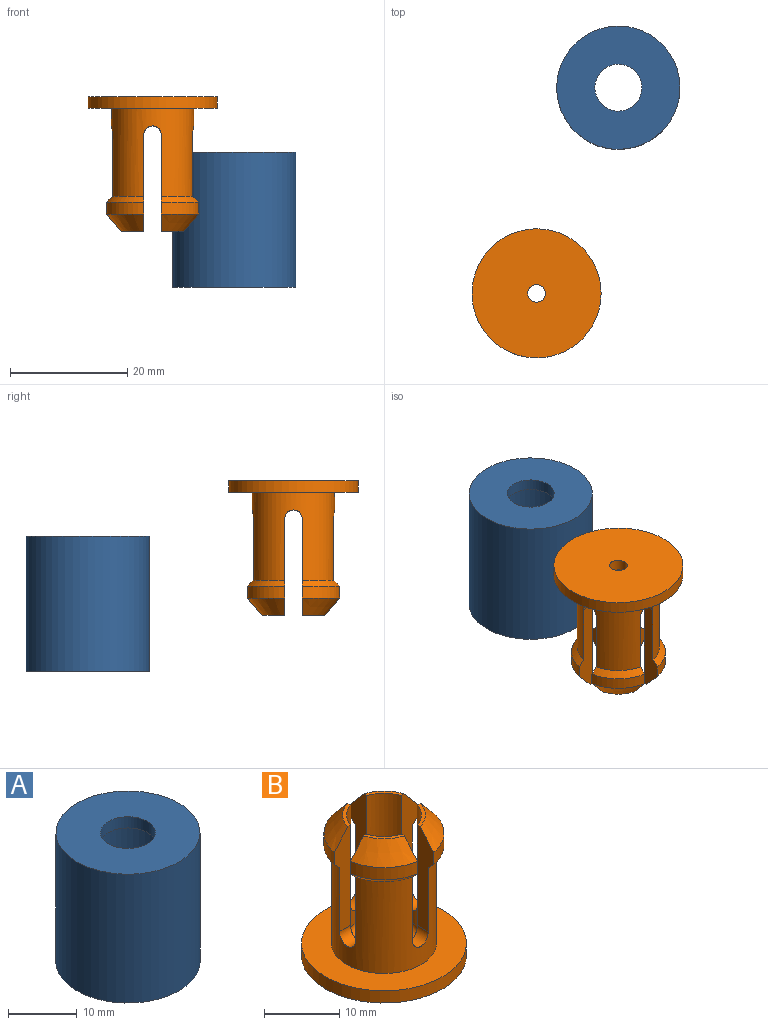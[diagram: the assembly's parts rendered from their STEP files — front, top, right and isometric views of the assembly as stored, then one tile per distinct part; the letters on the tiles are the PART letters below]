
ASSEMBLY  parts=2 mates=1
PART A: 10 faces, bbox 21x21x23 mm
  f0: cone r=7mm half-angle=45deg, axis (0,0,-1), area 103.3mm2, adj f1,f9
  f1: cylinder r=7mm len=14mm, axis (0,0,-1), area 263.9mm2, adj f0,f2
  f2: plane 14x14mm, normal (0,0,-1), area 103.7mm2, adj f1,f3
  f3: cylinder r=4mm len=8mm, axis (0,0,-1), area 50.3mm2, adj f2,f4
  f4: plane 21x21mm, normal (0,0,1), area 296.1mm2, adj f3,f5
  f5: cylinder r=10.5mm len=23mm, axis (0,0,-1), area 1517.4mm2, adj f4,f6
  f6: plane 21x21mm, normal (0,0,-1), area 192.4mm2, adj f5,f7
  f7: cylinder r=7mm len=14mm, axis (0,0,-1), area 439.8mm2, adj f6,f8
  f8: cone r=8.5mm half-angle=45deg, axis (0,0,1), area 103.3mm2, adj f7,f9
  f9: cylinder r=8.5mm len=17mm, axis (0,0,-1), area 106.8mm2, adj f0,f8
PART B: 36 faces, bbox 22.4x22.4x23.3 mm
  f0: cylinder r=5mm len=19.94mm, axis (0,0,-1), area 412mm2, adj f1,f6,f10,f14,f15,f24,f25,f26
  f1: plane 3.83x3.83mm, normal (0,0,1), area 2.8mm2, adj f0,f2,f28,f34
  f2: cone r=5.53mm half-angle=40deg, axis (0,0,-1), area 28.9mm2, adj f1,f3,f28,f34
  f3: cylinder r=8mm len=6.36mm, axis (0,0,-1), area 19.1mm2, adj f2,f4,f28,f34
  f4: cone r=8mm half-angle=45deg, axis (0,0,1), area 12.4mm2, adj f3,f5,f28,f34
  f5: cylinder r=7mm len=15mm, axis (0,0,-1), area 518.6mm2, adj f4,f9,f13,f18,f19,f24,f25,f26
  f6: plane 3.83x3.82mm, normal (0,0,1), area 2.8mm2, adj f0,f7,f29,f31
  f7: cone r=5.53mm half-angle=40deg, axis (0,0,-1), area 28.9mm2, adj f6,f8,f29,f31
  f8: cylinder r=8mm len=6.36mm, axis (0,0,-1), area 19.1mm2, adj f7,f9,f29,f31
  f9: cone r=8mm half-angle=45deg, axis (0,0,1), area 12.4mm2, adj f5,f8,f29,f31
  f10: plane 3.83x3.82mm, normal (0,0,1), area 2.8mm2, adj f0,f11,f24,f35
  f11: cone r=5.53mm half-angle=40deg, axis (0,0,-1), area 28.9mm2, adj f10,f12,f24,f35
  f12: cylinder r=8mm len=6.36mm, axis (0,0,-1), area 19.1mm2, adj f11,f13,f24,f35
  f13: cone r=8mm half-angle=45deg, axis (0,0,1), area 12.4mm2, adj f5,f12,f24,f35
  f14: torus R=4mm, axis (0,0,-1), area 45.8mm2, adj f0,f23
  f15: plane 3.82x3.82mm, normal (0,0,1), area 2.8mm2, adj f0,f16,f25,f30
  f16: cone r=5.53mm half-angle=40deg, axis (0,0,-1), area 28.9mm2, adj f15,f17,f25,f30
  f17: cylinder r=8mm len=6.36mm, axis (0,0,-1), area 19.1mm2, adj f16,f18,f25,f30
  f18: cone r=8mm half-angle=45deg, axis (0,0,1), area 12.4mm2, adj f5,f17,f25,f30
  f19: plane 22x22mm, normal (0,0,1), area 226.2mm2, adj f5,f20
  f20: cylinder r=11mm len=22mm, axis (0,0,-1), area 138.2mm2, adj f19,f21
  f21: plane 22x22mm, normal (0,0,-1), area 373.1mm2, adj f20,f22
  f22: cylinder r=1.5mm len=3mm, axis (0,0,-1), area 18.8mm2, adj f21,f23
  f23: plane 8x8mm, normal (0,0,1), area 43.2mm2, adj f14,f22
  f24: plane 16.74x3.46mm, normal (0,-1,0), area 35.7mm2, adj f0,f5,f10,f11,f12,f13,f26
  f25: plane 16.77x3.46mm, normal (0,1,0), area 35.7mm2, adj f0,f5,f15,f16,f17,f18,f26
  f26: cylinder r=1.5mm len=3mm, axis (-1,0,0), area 9.8mm2, adj f0,f5,f24,f25
  f27: cylinder r=1.5mm len=3mm, axis (-1,0,0), area 9.8mm2, adj f0,f5,f28,f29
  f28: plane 16.74x3.46mm, normal (0,-1,0), area 35.7mm2, adj f0,f1,f2,f3,f4,f5,f27
  f29: plane 16.77x3.46mm, normal (0,1,0), area 35.7mm2, adj f0,f5,f6,f7,f8,f9,f27
  f30: plane 16.77x3.46mm, normal (-1,0,0), area 35.7mm2, adj f0,f5,f15,f16,f17,f18,f32
  f31: plane 16.74x3.46mm, normal (1,0,0), area 35.7mm2, adj f0,f5,f6,f7,f8,f9,f32
  f32: cylinder r=1.5mm len=3mm, axis (0,-1,0), area 10mm2, adj f0,f5,f30,f31
  f33: cylinder r=1.5mm len=3mm, axis (0,-1,0), area 9.8mm2, adj f0,f5,f34,f35
  f34: plane 16.74x3.46mm, normal (1,0,0), area 35.7mm2, adj f0,f1,f2,f3,f4,f5,f33
  f35: plane 16.77x3.46mm, normal (-1,0,0), area 35.7mm2, adj f0,f5,f10,f11,f12,f13,f33
PLACE A t=(20.1,33.88,-39.3)mm
PLACE B rot(axis=(0,1,0),180deg) t=(6.17,-1.19,-3.13)mm
MATE planar B.f4 <-> A.f0  axis (0,0,1) through (6.17,-1.19,-16.3)mm
